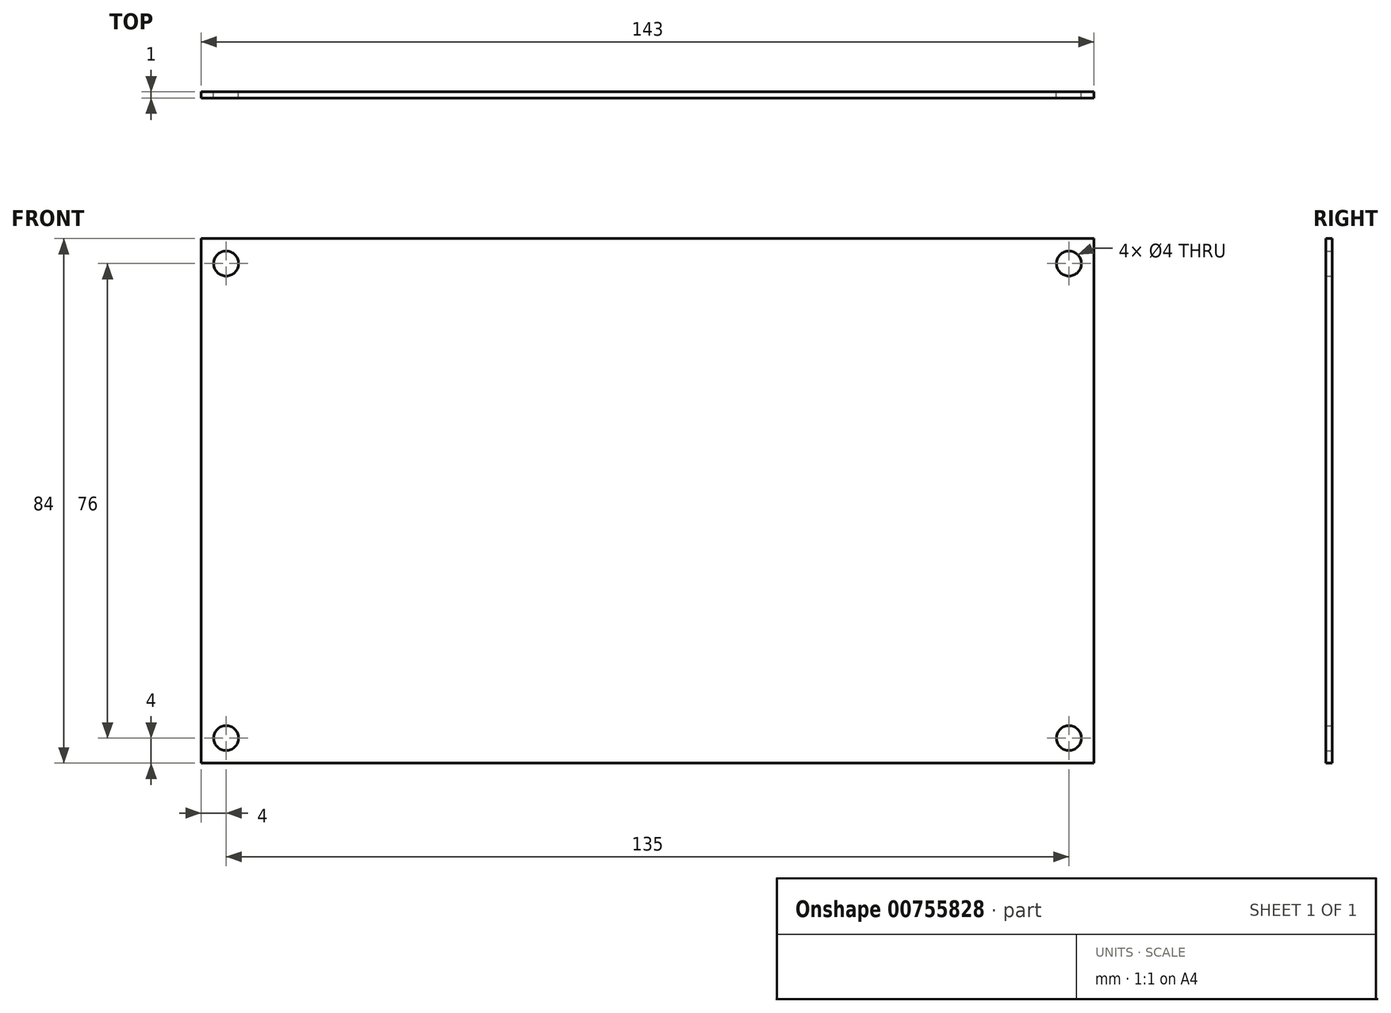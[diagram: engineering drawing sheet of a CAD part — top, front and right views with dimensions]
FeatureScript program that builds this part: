
annotation { "Feature Type Name" : "Feature", "Feature Type Description" : "" }
export const myFeature = defineFeature(function(context is Context, id is Id, definition is map)
    precondition{}
    {
        {
            var Q0;
            Q0=qCreatedBy(makeId("Front.planeOp"),FACE);
            var sketch = newSketch(context, id + "F0", { "sketchPlane" : qUnion([Q0])});
            skLineSegment(sketch, "E0.bottom", {"start": v(-71.5, -42) * mm, "end": v(71.5, -42) * mm});
            skLineSegment(sketch, "E0.top", {"start": v(-71.5, 42) * mm, "end": v(71.5, 42) * mm});
            skLineSegment(sketch, "E0.left", {"start": v(-71.5, -42) * mm, "end": v(-71.5, 42) * mm});
            skLineSegment(sketch, "E0.right", {"start": v(71.5, -42) * mm, "end": v(71.5, 42) * mm});
            skCircle(sketch, "E1", {"center": v(-67.5, -38) * mm, "radius": 2 * mm});
            skCircle(sketch, "E2.0.1.0", {"center": v(-67.5, 38) * mm, "radius": 2 * mm});
            skCircle(sketch, "E2.1.0.0", {"center": v(67.5, -38) * mm, "radius": 2 * mm});
            skCircle(sketch, "E2.1.1.0", {"center": v(67.5, 38) * mm, "radius": 2 * mm});
            skLineSegment(sketch, "E2.direction1", {"start": v(-67.5, -38) * mm, "end": v(67.5, -38) * mm, "construction": true});
            skLineSegment(sketch, "E2.direction2", {"start": v(-67.5, -38) * mm, "end": v(-67.5, 38) * mm, "construction": true});
            skSolve(sketch);
        }
        {
            var Q0;
            Q0=makeQuery(id+"F0.imprint","IMPRINT",FACE,{"disambiguationData":[TD([[makeQuery(id+"F0.imprint","IMPRINT",EDGE,{"derivedFrom":sQuery(id+"F0.wireOp",EDGE,"E0.bottom")}),1.0]])]});
            extrude(context, id + "F1", {"entities" : qUnion([Q0]), "depth" : 1 * mm, "offsetDistance" : 25 * mm});
        }
    });
